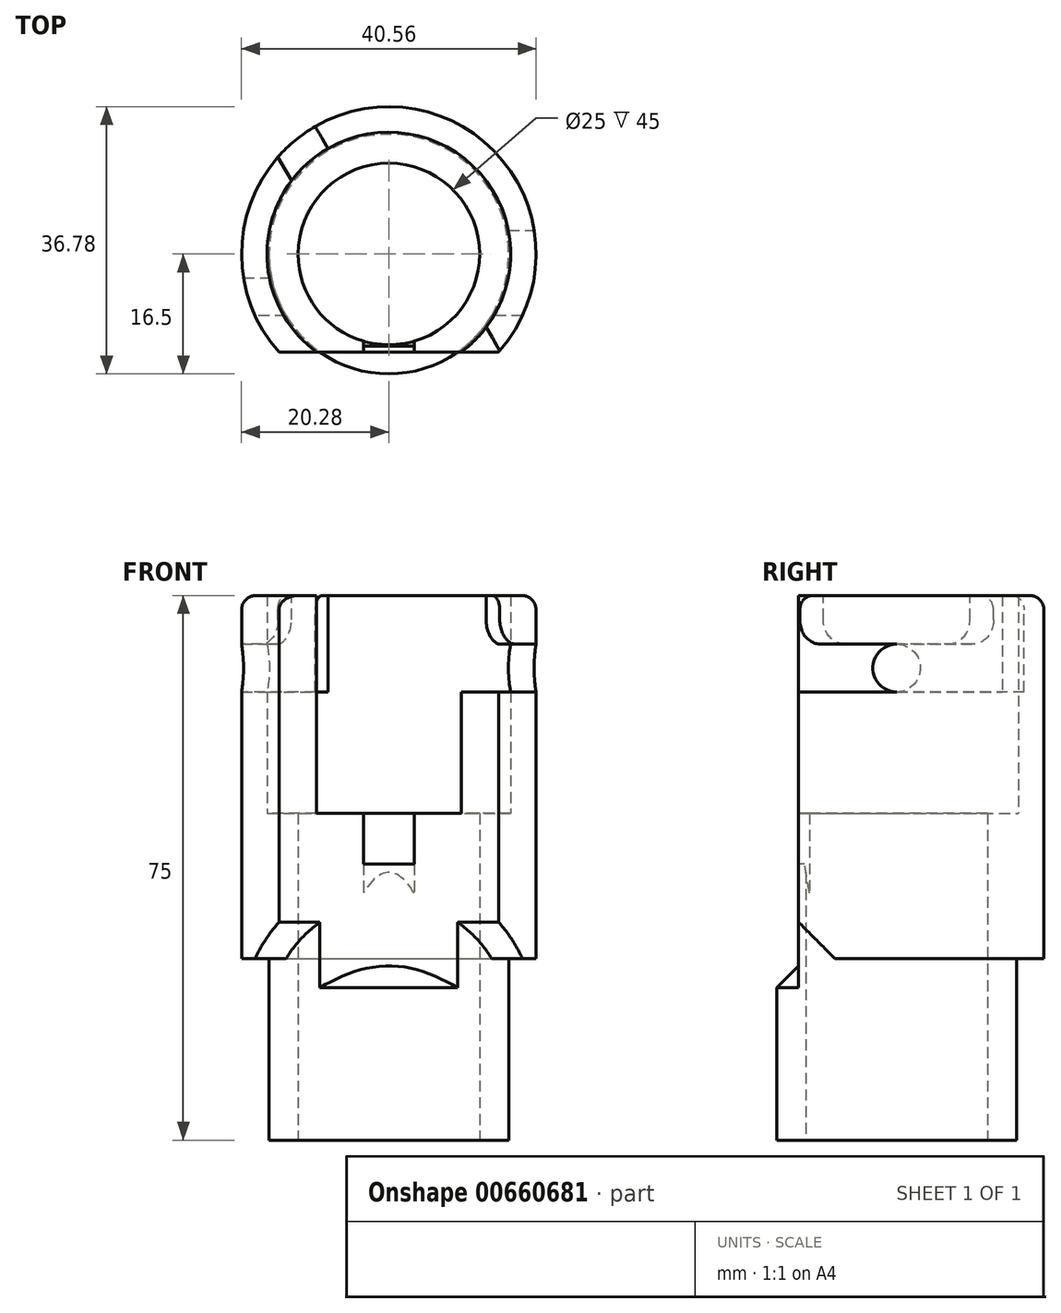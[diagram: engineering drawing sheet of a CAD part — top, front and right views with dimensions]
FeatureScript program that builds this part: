
annotation { "Feature Type Name" : "Feature", "Feature Type Description" : "" }
export const myFeature = defineFeature(function(context is Context, id is Id, definition is map)
    precondition{}
    {
        {
            var Q0;
            Q0=qCreatedBy(makeId("Front.planeOp"),FACE);
            var sketch = newSketch(context, id + "F0", { "sketchPlane" : qUnion([Q0])});
            skLineSegment(sketch, "E0", {"start": v(0, 0) * mm, "end": v(0, 49.07) * mm, "construction": true});
            skLineSegment(sketch, "E1", {"start": v(16.77, 50) * mm, "end": v(16.77, 20) * mm});
            skLineSegment(sketch, "E2", {"start": v(16.77, 20) * mm, "end": v(12.5, 20) * mm});
            skLineSegment(sketch, "E3", {"start": v(12.5, 20) * mm, "end": v(12.5, 0) * mm});
            skLineSegment(sketch, "E4", {"start": v(12.5, 0) * mm, "end": v(20.27, 0) * mm});
            skLineSegment(sketch, "E5", {"start": v(20.27, 0) * mm, "end": v(20.27, 50) * mm});
            skLineSegment(sketch, "E6", {"start": v(20.27, 50) * mm, "end": v(16.77, 50) * mm});
            skSolve(sketch);
        }
        {
            var Q0;
            Q0 = qSketchRegion(id + "F0", true);
            var Q1;
            Q1=sQuery(id+"F0.wireOp",EDGE,"E0");
            revolve(context, id + "F1", {"entities" : qUnion([Q0]), "axis" : qUnion([Q1]), "revolveType" : RevolveType.FULL});
        }
        {
            var Q0;
            Q0=qCreatedBy(makeId("Right.planeOp"),FACE);
            var sketch = newSketch(context, id + "F2", { "sketchPlane" : qUnion([Q0])});
            skCircle(sketch, "E7", {"center": v(0, 40) * mm, "radius": 3.28 * mm});
            skSolve(sketch);
        }
        {
            var Q0;
            Q0 = qSketchRegion(id + "F2", true);
            extrude(context, id + "F3", {"entities" : qUnion([Q0]), "operationType" : NewBodyOperationType.REMOVE, "endBound" : BoundingType.SYMMETRIC, "oppositeDirection" : true, "depth" : 50 * mm, "offsetDistance" : 25 * mm});
        }
        {
            var Q0;
            Q0=qCreatedBy(makeId("Front.planeOp"),FACE);
            var sketch = newSketch(context, id + "F4", { "sketchPlane" : qUnion([Q0])});
            skLineSegment(sketch, "E8.bottom", {"start": v(20.27, 36.73) * mm, "end": v(16.27, 36.73) * mm});
            skLineSegment(sketch, "E8.top", {"start": v(20.27, 43.27) * mm, "end": v(16.27, 43.27) * mm});
            skLineSegment(sketch, "E8.left", {"start": v(20.27, 36.73) * mm, "end": v(20.27, 43.27) * mm});
            skLineSegment(sketch, "E8.right", {"start": v(16.27, 36.73) * mm, "end": v(16.27, 43.27) * mm});
            skLineSegment(sketch, "E9", {"start": v(0, 0) * mm, "end": v(0, 50.33) * mm, "construction": true});
            skSolve(sketch);
        }
        {
            var Q0;
            Q0 = qSketchRegion(id + "F4", true);
            var Q1;
            Q1=sQuery(id+"F4.wireOp",EDGE,"E9");
            revolve(context, id + "F5", {"operationType" : NewBodyOperationType.REMOVE, "entities" : qUnion([Q0]), "axis" : qUnion([Q1]), "revolveType" : RevolveType.ONE_DIRECTION, "oppositeDirection" : true, "angle" : 60 * degree});
        }
        {
            var Q0;
            Q0=qCreatedBy(makeId("Front.planeOp"),FACE);
            var sketch = newSketch(context, id + "F6", { "sketchPlane" : qUnion([Q0])});
            skLineSegment(sketch, "E10.bottom", {"start": v(-20.27, 36.73) * mm, "end": v(-16.28, 36.73) * mm});
            skLineSegment(sketch, "E10.top", {"start": v(-20.27, 43.27) * mm, "end": v(-16.28, 43.27) * mm});
            skLineSegment(sketch, "E10.left", {"start": v(-20.27, 36.73) * mm, "end": v(-20.27, 43.27) * mm});
            skLineSegment(sketch, "E10.right", {"start": v(-16.28, 36.73) * mm, "end": v(-16.28, 43.27) * mm});
            skLineSegment(sketch, "E11", {"start": v(0, -2.52) * mm, "end": v(0, 49.59) * mm, "construction": true});
            skSolve(sketch);
        }
        {
            var Q0;
            Q0 = qSketchRegion(id + "F6", true);
            var Q1;
            Q1=sQuery(id+"F6.wireOp",EDGE,"E11");
            revolve(context, id + "F7", {"operationType" : NewBodyOperationType.REMOVE, "entities" : qUnion([Q0]), "axis" : qUnion([Q1]), "revolveType" : RevolveType.ONE_DIRECTION, "oppositeDirection" : true, "angle" : 60 * degree});
        }
        {
            var Q0;
            Q0=makeQuery(id+"F1.opRevolve","SWEPT_FACE",FACE,{"disambiguationData":[OSD([sQuery(id+"F0.wireOp",EDGE,"E6")])]});
            var sketch = newSketch(context, id + "F8", { "sketchPlane" : qUnion([Q0])});
            skLineSegment(sketch, "E12", {"start": v(-10.14, 17.56) * mm, "end": v(-8.39, 14.53) * mm});
            skArc(sketch, "E13", {"start": v(-10.14, 17.56) * mm, "mid": v(-12.88, 15.66) * mm, "end": v(-15.27, 13.34) * mm});
            skArc(sketch, "E14", {"start": v(-8.39, 14.53) * mm, "mid": v(-11.11, 12.57) * mm, "end": v(-13.4, 10.1) * mm});
            skArc(sketch, "E15", {"start": v(10.14, -17.56) * mm, "mid": v(12.88, -15.66) * mm, "end": v(15.27, -13.34) * mm});
            skArc(sketch, "E16", {"start": v(8.39, -14.53) * mm, "mid": v(11.11, -12.57) * mm, "end": v(13.4, -10.1) * mm});
            skLineSegment(sketch, "E17", {"start": v(13.4, -10.1) * mm, "end": v(15.27, -13.34) * mm});
            skLineSegment(sketch, "E18", {"start": v(-15.27, 13.34) * mm, "end": v(-13.4, 10.1) * mm});
            skLineSegment(sketch, "E19.trimOffspring", {"start": v(8.39, -14.53) * mm, "end": v(10.14, -17.56) * mm});
            skSolve(sketch);
        }
        {
            var Q0;
            Q0 = qSketchRegion(id + "F8", true);
            extrude(context, id + "F9", {"entities" : qUnion([Q0]), "operationType" : NewBodyOperationType.REMOVE, "oppositeDirection" : true, "depth" : 10 * mm, "offsetDistance" : 25 * mm});
        }
        {
            var Q0;
            Q0=makeQuery(id+"F9.boolean.opBoolean","SPLIT",FACE,{"disambiguationData":[TD([makeQuery(id+"F9.opExtrude","SWEPT_FACE",FACE,{"disambiguationData":[OSD([sQuery(id+"F8.wireOp",EDGE,"E18")])]})])],"derivedFrom":makeQuery(id+"F1.opRevolve","SWEPT_FACE",FACE,{"disambiguationData":[OSD([sQuery(id+"F0.wireOp",EDGE,"E6")])]})});
            var sketch = newSketch(context, id + "F10", { "sketchPlane" : qUnion([Q0])});
            skLineSegment(sketch, "E20.bottom", {"start": v(-16, -21.5) * mm, "end": v(16, -21.5) * mm});
            skLineSegment(sketch, "E20.top", {"start": v(-16, -13.5) * mm, "end": v(16, -13.5) * mm});
            skLineSegment(sketch, "E20.left", {"start": v(-16, -21.5) * mm, "end": v(-16, -13.5) * mm});
            skLineSegment(sketch, "E20.right", {"start": v(16, -21.5) * mm, "end": v(16, -13.5) * mm});
            skSolve(sketch);
        }
        {
            var Q0;
            Q0 = qSketchRegion(id + "F10", true);
            extrude(context, id + "F11", {"entities" : qUnion([Q0]), "operationType" : NewBodyOperationType.REMOVE, "endBound" : BoundingType.THROUGH_ALL, "oppositeDirection" : true, "depth" : 25 * mm, "offsetDistance" : 25 * mm});
        }
        {
            var Q0;
            Q0=makeQuery(id+"F11.boolean.opBoolean","COPY",FACE,{"derivedFrom":makeQuery(id+"F11.opExtrude","SWEPT_FACE",FACE,{"disambiguationData":[OSD([sQuery(id+"F10.wireOp",EDGE,"E20.top")])]})});
            var sketch = newSketch(context, id + "F12", { "sketchPlane" : qUnion([Q0])});
            skLineSegment(sketch, "E21.bottom", {"start": v(3.5, 20) * mm, "end": v(-3.5, 20) * mm});
            skLineSegment(sketch, "E21.top", {"start": v(3.5, 13) * mm, "end": v(-3.5, 13) * mm});
            skLineSegment(sketch, "E21.left", {"start": v(3.5, 20) * mm, "end": v(3.5, 13) * mm});
            skLineSegment(sketch, "E21.right", {"start": v(-3.5, 20) * mm, "end": v(-3.5, 13) * mm});
            skPoint(sketch, "E21.middle", {"position": v(0, 16.5) * mm});
            skSolve(sketch);
        }
        {
            var Q0;
            Q0 = qSketchRegion(id + "F12", true);
            extrude(context, id + "F13", {"entities" : qUnion([Q0]), "operationType" : NewBodyOperationType.REMOVE, "oppositeDirection" : true, "depth" : 5 * mm, "offsetDistance" : 25 * mm});
        }
        {
            var Q0;
            Q0=qCreatedBy(makeId("Right.planeOp"),FACE);
            var sketch = newSketch(context, id + "F14", { "sketchPlane" : qUnion([Q0])});
            skLineSegment(sketch, "E22", {"start": v(-12.7, 13) * mm, "end": v(-10.3, 13) * mm});
            skLineSegment(sketch, "E23", {"start": v(-10.3, 13) * mm, "end": v(-10.3, 5) * mm});
            skLineSegment(sketch, "E24", {"start": v(-10.3, 5) * mm, "end": v(-11.29, 5) * mm});
            skLineSegment(sketch, "E25", {"start": v(-11.29, 5) * mm, "end": v(-12.7, 13) * mm});
            skSolve(sketch);
        }
        {
            var Q0;
            Q0 = qSketchRegion(id + "F14", true);
            extrude(context, id + "F15", {"entities" : qUnion([Q0]), "operationType" : NewBodyOperationType.REMOVE, "endBound" : BoundingType.SYMMETRIC, "depth" : 7 * mm, "offsetDistance" : 25 * mm});
        }
        {
            var Q0;
            {var subQ0=sQuery(id+"F0.wireOp",EDGE,"E6");var subQ1=sQuery(id+"F0.wireOp",EDGE,"E5");Q0=makeQuery(id+"F9.boolean.opBoolean","SPLIT",EDGE,{"disambiguationData":[TD([makeQuery(id+"F9.opExtrude","SWEPT_FACE",FACE,{"disambiguationData":[OSD([sQuery(id+"F8.wireOp",EDGE,"E12")])]})])],"derivedFrom":makeQuery(id+"F1.opRevolve","SWEPT_EDGE",EDGE,{"disambiguationData":[OSD([subQ1,subQ0])]})});}
            var Q1;
            {var subQ0=sQuery(id+"F0.wireOp",EDGE,"E5");var subQ1=sQuery(id+"F0.wireOp",EDGE,"E6");Q1=makeQuery(id+"F9.boolean.opBoolean","SPLIT",EDGE,{"disambiguationData":[TD([makeQuery(id+"F9.opExtrude","SWEPT_FACE",FACE,{"disambiguationData":[OSD([sQuery(id+"F8.wireOp",EDGE,"E18")])]})])],"derivedFrom":makeQuery(id+"F1.opRevolve","SWEPT_EDGE",EDGE,{"disambiguationData":[OSD([subQ0,subQ1])]})});}
            fillet(context, id + "F16", {"entities" : qUnion([Q0, Q1]), "radius" : 2 * mm, "tangentPropagation" : true, "allowEdgeOverflow" : false});
        }
        {
            var Q0;
            Q0=makeQuery(id+"F9.boolean.opBoolean","INTERSECT",EDGE,{"derivedFrom":[makeQuery(id+"F7.boolean.opBoolean","COPY",FACE,{"derivedFrom":makeQuery(id+"F7.opRevolve","SWEPT_FACE",FACE,{"disambiguationData":[OSD([sQuery(id+"F6.wireOp",EDGE,"E10.top")])]})}),makeQuery(id+"F9.opExtrude","SWEPT_FACE",FACE,{"disambiguationData":[OSD([sQuery(id+"F8.wireOp",EDGE,"E18")])]})]});
            var Q1;
            Q1=makeQuery(id+"F9.boolean.opBoolean","INTERSECT",EDGE,{"derivedFrom":[makeQuery(id+"F5.boolean.opBoolean","COPY",FACE,{"derivedFrom":makeQuery(id+"F5.opRevolve","SWEPT_FACE",FACE,{"disambiguationData":[OSD([sQuery(id+"F4.wireOp",EDGE,"E8.top")])]})}),makeQuery(id+"F9.opExtrude","SWEPT_FACE",FACE,{"disambiguationData":[OSD([sQuery(id+"F8.wireOp",EDGE,"E17")])]})]});
            fillet(context, id + "F17", {"entities" : qUnion([Q0, Q1]), "radius" : 3.4 * mm, "tangentPropagation" : true, "allowEdgeOverflow" : false});
        }
        {
            var Q0;
            Q0=makeQuery(id+"F1.opRevolve","SWEPT_FACE",FACE,{"disambiguationData":[OSD([sQuery(id+"F0.wireOp",EDGE,"E4")])]});
            var sketch = newSketch(context, id + "F18", { "sketchPlane" : qUnion([Q0])});
            skCircle(sketch, "E26", {"center": v(0, 0) * mm, "radius": 12.5 * mm});
            skCircle(sketch, "E27", {"center": v(0, 0) * mm, "radius": 16.5 * mm});
            skSolve(sketch);
        }
        {
            var Q0;
            Q0 = qSketchRegion(id + "F18", true);
            extrude(context, id + "F19", {"entities" : qUnion([Q0]), "operationType" : NewBodyOperationType.ADD, "depth" : 25 * mm, "offsetDistance" : 25 * mm});
        }
        {
            var Q0;
            {var subQ0=sQuery(id+"F18.wireOp",EDGE,"E27");Q0=makeQuery(id+"F19.boolean.opBoolean","SPLIT",EDGE,{"disambiguationData":[topologyDisambiguationEdgeConnected([makeQuery(id+"F1.opRevolve","SWEPT_FACE",FACE,{"disambiguationData":[OSD([sQuery(id+"F0.wireOp",EDGE,"E4")])]})])],"derivedFrom":makeQuery(id+"F19.opExtrude","CAP_EDGE",EDGE,{"disambiguationData":[OSD([subQ0])],"isStart":true})});}
            chamfer(context, id + "F20", {"entities" : qUnion([Q0]), "width" : 4 * mm, "tangentPropagation" : true});
        }
        {
            var Q0;
            {var subQ0=makeQuery(id+"F11.opExtrude","SWEPT_FACE",FACE,{"disambiguationData":[OSD([sQuery(id+"F10.wireOp",EDGE,"E20.top")])]});Q0=makeQuery(id+"F19.boolean.opBoolean","SPLIT",EDGE,{"disambiguationData":[topologyDisambiguationEdgeConnected([makeQuery(id+"F11.boolean.opBoolean","COPY",FACE,{"derivedFrom":subQ0}),makeQuery(id+"F19.opExtrude","CAP_FACE",FACE,{"disambiguationData":[OSD([sQuery(id+"F18.wireOp",EDGE,"E26"),sQuery(id+"F18.wireOp",EDGE,"E27")])],"isStart":true})])],"derivedFrom":makeQuery(id+"F11.boolean.opBoolean","INTERSECT",EDGE,{"derivedFrom":[makeQuery(id+"F1.opRevolve","SWEPT_FACE",FACE,{"disambiguationData":[OSD([sQuery(id+"F0.wireOp",EDGE,"E4")])]}),subQ0]})});}
            chamfer(context, id + "F21", {"entities" : qUnion([Q0]), "width" : 5 * mm, "tangentPropagation" : true});
        }
    });
